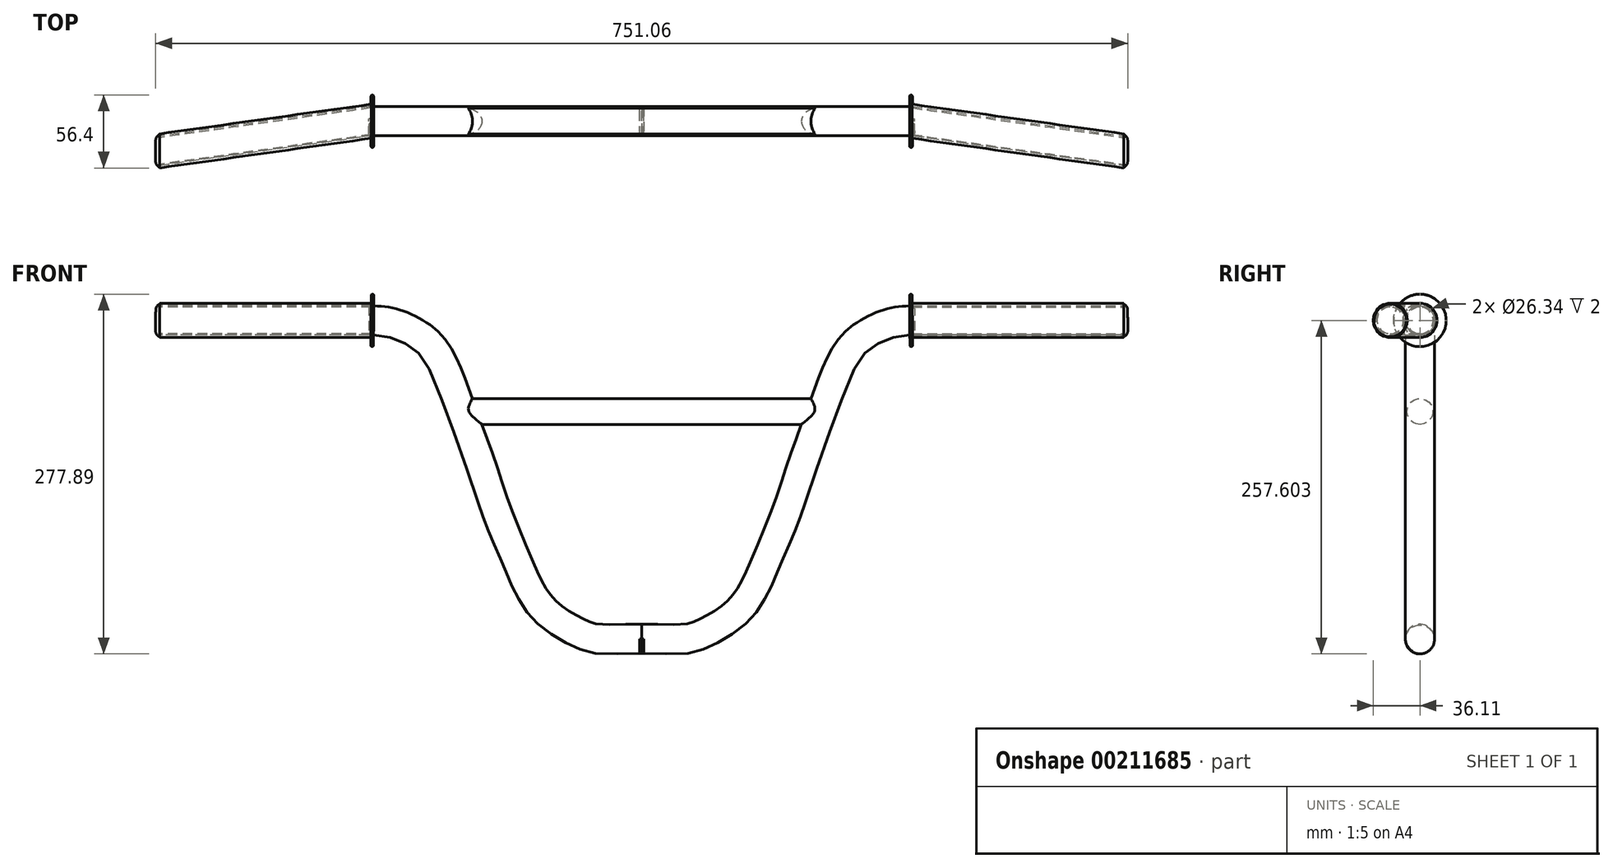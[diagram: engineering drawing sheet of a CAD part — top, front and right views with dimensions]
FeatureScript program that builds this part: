
annotation { "Feature Type Name" : "Feature", "Feature Type Description" : "" }
export const myFeature = defineFeature(function(context is Context, id is Id, definition is map)
    precondition{}
    {
        {
            var Q0;
            Q0=qCreatedBy(makeId("Right.planeOp"),FACE);
            var sketch = newSketch(context, id + "F0", { "sketchPlane" : qUnion([Q0])});
            skCircle(sketch, "E0", {"center": v(0, 0) * mm, "radius": 11.25 * mm});
            skSolve(sketch);
        }
        {
            var Q0;
            Q0=qCreatedBy(makeId("Front.planeOp"),FACE);
            var sketch = newSketch(context, id + "F1", { "sketchPlane" : qUnion([Q0])});
            skFitSpline(sketch, "E1", {"points": [v(-1.5, 0) * mm, v(15.86, 0) * mm, v(34.1, 0) * mm, v(47.71, 4.4) * mm, v(66.82, 15.25) * mm, v(79.56, 27.55) * mm, v(89.84, 45.07) * mm, v(97.08, 62.16) * mm, v(109.38, 91.4) * mm, v(123.57, 132.8) * mm, v(143.12, 186.95) * mm, v(156.87, 218.95) * mm, v(170.19, 233.57) * mm, v(192.05, 244.14) * mm, v(210.73, 246.17) * mm], "startDerivative": vector(266.06, 4.58) * mm, "endDerivative": vector(289.76, 6.71) * mm});
            skSolve(sketch);
        }
        {
            var Q0;
            Q0=makeQuery(id+"F0.imprint","IMPRINT",FACE,{"disambiguationData":[TD([[makeQuery(id+"F0.imprint","IMPRINT",EDGE,{"derivedFrom":sQuery(id+"F0.wireOp",EDGE,"E0")}),1.0]])]});
            var Q1;
            Q1=sQuery(id+"F1.wireOp",EDGE,"E1");
            sweep(context, id + "F2", {"profiles" : qUnion([Q0]), "path" : qUnion([Q1])});
        }
        {
            var Q0;
            Q0=qCreatedBy(makeId("Top.planeOp"),FACE);
            var sketch = newSketch(context, id + "F3", { "sketchPlane" : qUnion([Q0])});
            skEllipse(sketch, "E2.0.0", {"center": v(210.73, 0) * mm, "majorRadius": 11.25 * mm, "minorRadius": 0.07 * mm, "majorAxis": v(0, -1), "construction": true});
            skLineSegment(sketch, "E3", {"start": v(210.73, 0) * mm, "end": v(374.1, -22.94) * mm});
            skSolve(sketch);
        }
        {
            var Q0;
            Q0=makeQuery(id+"F2.opSweep","CAP_FACE",FACE,{"disambiguationData":[OSD([sQuery(id+"F0.wireOp",EDGE,"E0"),sQuery(id+"F1.wireOp",VERTEX,"E1.end")])],"isStart":false});
            var sketch = newSketch(context, id + "F4", { "sketchPlane" : qUnion([Q0])});
            skCircle(sketch, "E4.0.0", {"center": v(0, 244.75) * mm, "radius": 11.25 * mm});
            skSolve(sketch);
        }
        {
            var Q0;
            Q0=makeQuery(id+"F4.imprint","IMPRINT",FACE,{"disambiguationData":[TD([[makeQuery(id+"F4.imprint","IMPRINT",EDGE,{"derivedFrom":sQuery(id+"F4.wireOp",EDGE,"E4.0.0")}),1.0]])]});
            var Q1;
            Q1 = qConstructionFilter(qBodyType(qCreatedBy(id + "F3" ,EDGE), BodyType.WIRE), ConstructionObject.NO);
            sweep(context, id + "F5", {"operationType" : NewBodyOperationType.ADD, "profiles" : qUnion([Q0]), "path" : qUnion([Q1])});
        }
        {
            var Q0;
            Q0=qCreatedBy(makeId("Right.planeOp"),FACE);
            var sketch = newSketch(context, id + "F6", { "sketchPlane" : qUnion([Q0])});
            skCircle(sketch, "E5", {"center": v(0, 175.76) * mm, "radius": 10 * mm});
            skSolve(sketch);
        }
        {
            var Q0;
            Q0=qCreatedBy(makeId("Front.planeOp"),FACE);
            var sketch = newSketch(context, id + "F7", { "sketchPlane" : qUnion([Q0])});
            skLineSegment(sketch, "E6", {"start": v(0, 170.42) * mm, "end": v(138.11, 170.42) * mm});
            skSolve(sketch);
        }
        {
            var Q0;
            Q0=makeQuery(id+"F6.imprint","IMPRINT",FACE,{"disambiguationData":[TD([[makeQuery(id+"F6.imprint","IMPRINT",EDGE,{"derivedFrom":sQuery(id+"F6.wireOp",EDGE,"E5")}),1.0]])]});
            var Q1;
            Q1=sQuery(id+"F7.wireOp",EDGE,"E6");
            sweep(context, id + "F8", {"operationType" : NewBodyOperationType.ADD, "profiles" : qUnion([Q0]), "path" : qUnion([Q1])});
        }
        {
            var Q0;
            Q0=makeQuery(id+"F2.opSweep","SWEPT_BODY",BODY,{"disambiguationData":[OSD([sQuery(id+"F0.wireOp",EDGE,"E0"),sQuery(id+"F1.wireOp",EDGE,"E1")])]});
            var Q1;
            Q1=makeQuery(id+"F8.opSweep","CAP_FACE",FACE,{"disambiguationData":[OSD([sQuery(id+"F6.wireOp",EDGE,"E5"),sQuery(id+"F7.wireOp",VERTEX,"E6.start")])],"isStart":true});
            mirror(context, id + "F9", {"operationType" : NewBodyOperationType.ADD, "entities" : qUnion([Q0]), "mirrorPlane" : qUnion([Q1])});
        }
        {
            var Q0;
            Q0=makeQuery(id+"F5.opSweep","CAP_FACE",FACE,{"disambiguationData":[OSD([sQuery(id+"F3.wireOp",VERTEX,"609372c0-d08d-46cf-a803-6c95d84b4eb6.end"),sQuery(id+"F4.wireOp",EDGE,"E4.0.0")])],"isStart":false});
            var sketch = newSketch(context, id + "F10", { "sketchPlane" : qUnion([Q0])});
            skCircle(sketch, "E7", {"center": v(-22.94, 243.67) * mm, "radius": 10.31 * mm});
            skSolve(sketch);
        }
        {
            var Q0;
            Q0 = qSketchRegion(id + "F10", true);
            var Q1;
            Q1 = qConstructionFilter(qBodyType(qCreatedBy(id + "F3" ,EDGE), BodyType.WIRE), ConstructionObject.NO);
            sweep(context, id + "F11", {"operationType" : NewBodyOperationType.REMOVE, "profiles" : qUnion([Q0]), "path" : qUnion([Q1])});
        }
        {
            var Q0;
            Q0=makeQuery(id+"F2.opSweep","SWEPT_BODY",BODY,{"disambiguationData":[OSD([sQuery(id+"F0.wireOp",EDGE,"E0"),sQuery(id+"F1.wireOp",EDGE,"E1")])]});
            var Q1;
            Q1=qCreatedBy(makeId("Right.planeOp"),FACE);
            mirror(context, id + "F12", {"operationType" : NewBodyOperationType.INTERSECT, "entities" : qUnion([Q0]), "mirrorPlane" : qUnion([Q1])});
        }
        {
            var Q0;
            Q0=makeQuery(id+"F5.opSweep","CAP_FACE",FACE,{"disambiguationData":[OSD([sQuery(id+"F3.wireOp",VERTEX,"609372c0-d08d-46cf-a803-6c95d84b4eb6.end"),sQuery(id+"F4.wireOp",EDGE,"E4.0.0")])],"isStart":false});
            var sketch = newSketch(context, id + "F13", { "sketchPlane" : qUnion([Q0])});
            skCircle(sketch, "E8", {"center": v(-22.94, 243.67) * mm, "radius": 13.17 * mm});
            skSolve(sketch);
        }
        {
            var Q0;
            Q0=makeQuery(id+"F13.imprint","IMPRINT",FACE,{"disambiguationData":[TD([[makeQuery(id+"F13.imprint","IMPRINT",EDGE,{"derivedFrom":sQuery(id+"F13.wireOp",EDGE,"E8")}),1.0]])]});
            var Q1;
            Q1 = qConstructionFilter(qBodyType(qCreatedBy(id + "F3" ,EDGE), BodyType.WIRE), ConstructionObject.NO);
            sweep(context, id + "F14", {"profiles" : qUnion([Q0]), "path" : qUnion([Q1])});
        }
        {
            var Q0;
            Q0=makeQuery(id+"F14.opSweep","CAP_FACE",FACE,{"disambiguationData":[OSD([sQuery(id+"F3.wireOp",VERTEX,"609372c0-d08d-46cf-a803-6c95d84b4eb6.start"),sQuery(id+"F3.wireOp",VERTEX,"609372c0-d08d-46cf-a803-6c95d84b4eb6.end"),sQuery(id+"F4.wireOp",EDGE,"E4.0.0"),sQuery(id+"F13.wireOp",EDGE,"E8")])],"isStart":false});
            var sketch = newSketch(context, id + "F15", { "sketchPlane" : qUnion([Q0])});
            skCircle(sketch, "E9", {"center": v(0, 244.75) * mm, "radius": 20.29 * mm});
            skSolve(sketch);
        }
        {
            var Q0;
            Q0=makeQuery(id+"F15.imprint","IMPRINT",FACE,{"disambiguationData":[TD([[makeQuery(id+"F15.imprint","IMPRINT",EDGE,{"derivedFrom":sQuery(id+"F15.wireOp",EDGE,"E9")}),1.0]])]});
            extrude(context, id + "F16", {"entities" : qUnion([Q0]), "depth" : 2 * mm});
        }
        {
            var Q0;
            Q0=makeQuery(id+"F16.opExtrude","CAP_EDGE",EDGE,{"disambiguationData":[OSD([sQuery(id+"F15.wireOp",EDGE,"E9")])],"isStart":false});
            var Q1;
            Q1=makeQuery(id+"F16.opExtrude","CAP_EDGE",EDGE,{"disambiguationData":[OSD([sQuery(id+"F15.wireOp",EDGE,"E9")])],"isStart":true});
            fillet(context, id + "F17", {"entities" : qUnion([Q0, Q1]), "radius" : 1 * mm, "tangentPropagation" : true, "allowEdgeOverflow" : false});
        }
        {
            var Q0;
            Q0=makeQuery(id+"F14.opSweep","CAP_FACE",FACE,{"disambiguationData":[OSD([sQuery(id+"F3.wireOp",VERTEX,"609372c0-d08d-46cf-a803-6c95d84b4eb6.end"),sQuery(id+"F4.wireOp",EDGE,"E4.0.0"),sQuery(id+"F13.wireOp",EDGE,"E8")])],"isStart":true});
            var sketch = newSketch(context, id + "F18", { "sketchPlane" : qUnion([Q0])});
            skCircle(sketch, "E10", {"center": v(-22.94, 243.67) * mm, "radius": 12.64 * mm});
            skSolve(sketch);
        }
        {
            var Q0;
            Q0 = qSketchRegion(id + "F18", true);
            extrude(context, id + "F19", {"entities" : qUnion([Q0]), "depth" : 3 * mm});
        }
        {
            var Q0;
            Q0=makeQuery(id+"F19.opExtrude","CAP_EDGE",EDGE,{"disambiguationData":[OSD([sQuery(id+"F18.wireOp",EDGE,"E10")])],"isStart":false});
            fillet(context, id + "F20", {"entities" : qUnion([Q0]), "radius" : 5 * mm, "tangentPropagation" : true, "allowEdgeOverflow" : false});
        }
        {
            var Q0;
            Q0=makeQuery(id+"F14.opSweep","SWEPT_BODY",BODY,{"disambiguationData":[OSD([sQuery(id+"F3.wireOp",VERTEX,"609372c0-d08d-46cf-a803-6c95d84b4eb6.end"),sQuery(id+"F3.wireOp",EDGE,"609372c0-d08d-46cf-a803-6c95d84b4eb6"),sQuery(id+"F4.wireOp",EDGE,"E4.0.0"),sQuery(id+"F13.wireOp",EDGE,"E8")])]});
            var Q1;
            Q1=qCreatedBy(makeId("Right.planeOp"),FACE);
            mirror(context, id + "F21", {"entities" : qUnion([Q0]), "mirrorPlane" : qUnion([Q1])});
        }
        {
            var Q0;
            Q0=makeQuery(id+"F16.opExtrude","SWEPT_BODY",BODY,{"disambiguationData":[OSD([sQuery(id+"F3.wireOp",VERTEX,"609372c0-d08d-46cf-a803-6c95d84b4eb6.start"),sQuery(id+"F13.wireOp",EDGE,"E8"),sQuery(id+"F15.wireOp",EDGE,"E9")])]});
            var Q1;
            Q1=qCreatedBy(makeId("Right.planeOp"),FACE);
            mirror(context, id + "F22", {"entities" : qUnion([Q0]), "mirrorPlane" : qUnion([Q1])});
        }
        {
            var Q0;
            Q0=makeQuery(id+"F14.opSweep","SWEPT_BODY",BODY,{"disambiguationData":[OSD([sQuery(id+"F3.wireOp",VERTEX,"609372c0-d08d-46cf-a803-6c95d84b4eb6.end"),sQuery(id+"F3.wireOp",EDGE,"609372c0-d08d-46cf-a803-6c95d84b4eb6"),sQuery(id+"F4.wireOp",EDGE,"E4.0.0"),sQuery(id+"F13.wireOp",EDGE,"E8")])]});
            var Q1;
            Q1=qCreatedBy(makeId("Right.planeOp"),FACE);
            mirror(context, id + "F23", {"entities" : qUnion([Q0]), "mirrorPlane" : qUnion([Q1])});
        }
        {
            var Q0;
            Q0=makeQuery(id+"F23.opPattern","COPY",BODY,{"derivedFrom":makeQuery(id+"F14.opSweep","SWEPT_BODY",BODY,{"disambiguationData":[OSD([sQuery(id+"F3.wireOp",VERTEX,"609372c0-d08d-46cf-a803-6c95d84b4eb6.end"),sQuery(id+"F3.wireOp",EDGE,"609372c0-d08d-46cf-a803-6c95d84b4eb6"),sQuery(id+"F4.wireOp",EDGE,"E4.0.0"),sQuery(id+"F13.wireOp",EDGE,"E8")])]}),"instanceName":"1"});
            deleteBodies(context, id + "F24", {"entities" : qUnion([Q0])});
        }
        {
            var Q0;
            Q0=makeQuery(id+"F19.opExtrude","SWEPT_BODY",BODY,{"disambiguationData":[OSD([sQuery(id+"F18.wireOp",EDGE,"E10")])]});
            var Q1;
            Q1=qCreatedBy(makeId("Right.planeOp"),FACE);
            mirror(context, id + "F25", {"entities" : qUnion([Q0]), "mirrorPlane" : qUnion([Q1])});
        }
    });
